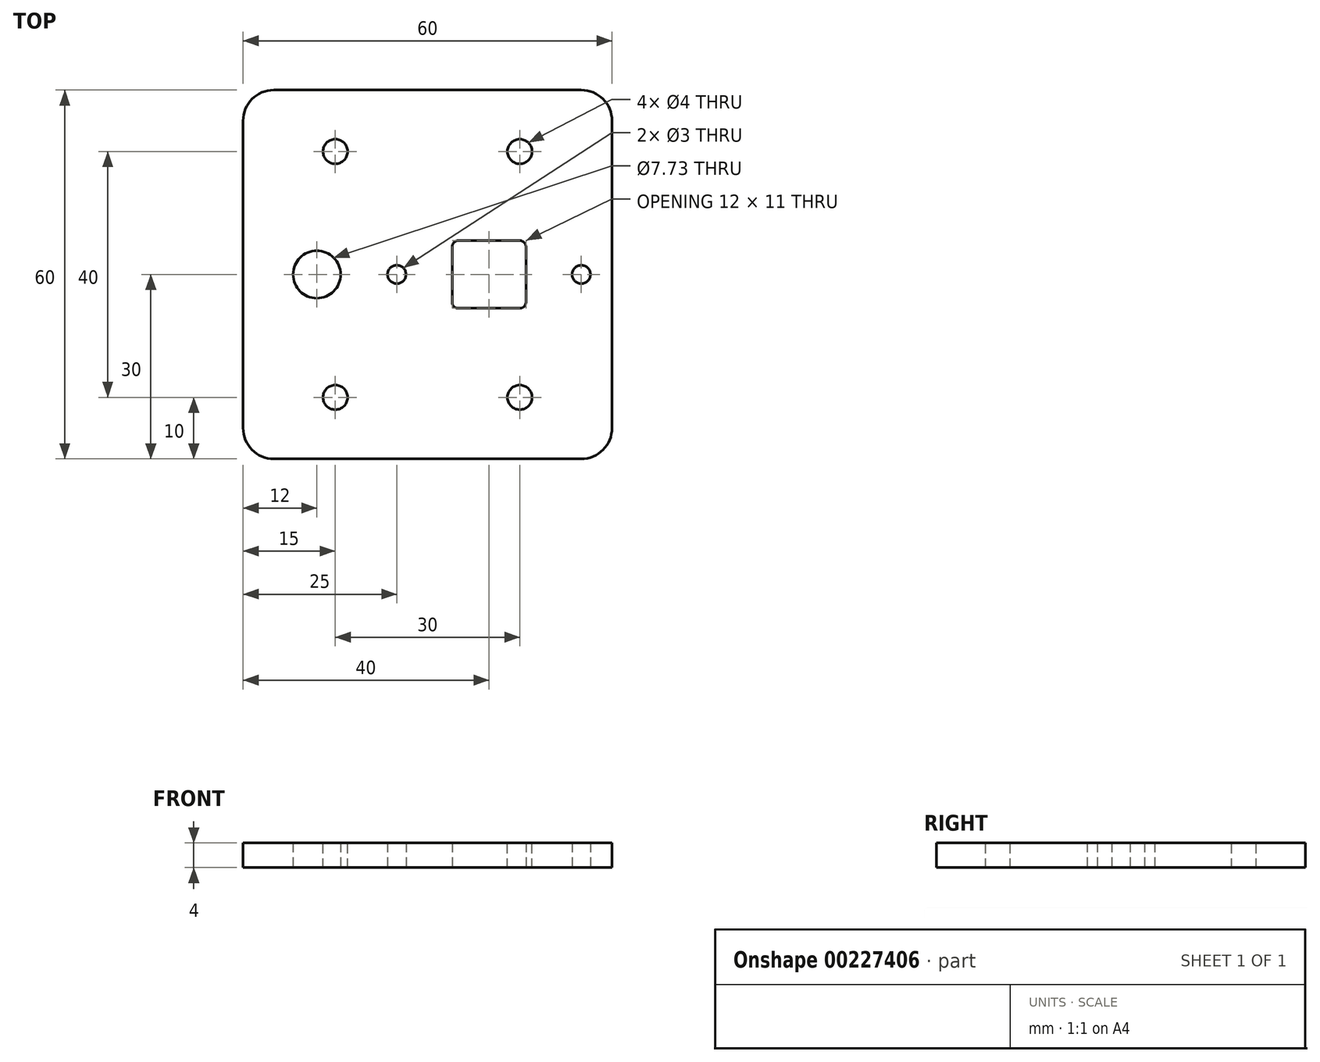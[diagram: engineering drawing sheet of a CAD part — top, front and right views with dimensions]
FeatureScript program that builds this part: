
annotation { "Feature Type Name" : "Feature", "Feature Type Description" : "" }
export const myFeature = defineFeature(function(context is Context, id is Id, definition is map)
    precondition{}
    {
        {
            var Q0;
            Q0=qCreatedBy(makeId("Top.planeOp"),FACE);
            var sketch = newSketch(context, id + "F0", { "sketchPlane" : qUnion([Q0])});
            skCircle(sketch, "E0", {"center": v(-18, 0) * mm, "radius": 3.86 * mm});
            skLineSegment(sketch, "E1.bottom", {"start": v(-30, 30) * mm, "end": v(30, 30) * mm});
            skLineSegment(sketch, "E1.top", {"start": v(-30, -30) * mm, "end": v(30, -30) * mm});
            skLineSegment(sketch, "E1.left", {"start": v(-30, 30) * mm, "end": v(-30, -30) * mm});
            skLineSegment(sketch, "E1.right", {"start": v(30, 30) * mm, "end": v(30, -30) * mm});
            skPoint(sketch, "E2", {"position": v(-30, 0) * mm});
            skPoint(sketch, "E3", {"position": v(0, 30) * mm});
            skCircle(sketch, "E4", {"center": v(-5, 0) * mm, "radius": 1.5 * mm});
            skCircle(sketch, "E5", {"center": v(25, 0) * mm, "radius": 1.5 * mm});
            skLineSegment(sketch, "E6.bottom", {"start": v(4, 5.5) * mm, "end": v(16, 5.5) * mm});
            skLineSegment(sketch, "E6.top", {"start": v(4, -5.5) * mm, "end": v(16, -5.5) * mm});
            skLineSegment(sketch, "E6.left", {"start": v(4, 5.5) * mm, "end": v(4, -5.5) * mm});
            skLineSegment(sketch, "E6.right", {"start": v(16, 5.5) * mm, "end": v(16, -5.5) * mm});
            skPoint(sketch, "E7", {"position": v(16, 0) * mm});
            skPoint(sketch, "E8", {"position": v(4, 0) * mm});
            skSolve(sketch);
        }
        {
            var Q0;
            Q0=makeQuery(id+"F0.imprint","IMPRINT",FACE,{"disambiguationData":[TD([[makeQuery(id+"F0.imprint","IMPRINT",EDGE,{"derivedFrom":sQuery(id+"F0.wireOp",EDGE,"E0")}),-1.0]])]});
            extrude(context, id + "F1", {"entities" : qUnion([Q0]), "depth" : 4 * mm});
        }
        {
            var Q0;
            Q0=makeQuery(id+"F1.opExtrude","CAP_FACE",FACE,{"disambiguationData":[OSD([sQuery(id+"F0.wireOp",EDGE,"E0"),sQuery(id+"F0.wireOp",EDGE,"E1.bottom"),sQuery(id+"F0.wireOp",EDGE,"E1.top"),sQuery(id+"F0.wireOp",EDGE,"E1.left"),sQuery(id+"F0.wireOp",EDGE,"E1.right"),sQuery(id+"F0.wireOp",EDGE,"E4"),sQuery(id+"F0.wireOp",EDGE,"E5"),sQuery(id+"F0.wireOp",EDGE,"E6.bottom"),sQuery(id+"F0.wireOp",EDGE,"E6.top"),sQuery(id+"F0.wireOp",EDGE,"E6.left"),sQuery(id+"F0.wireOp",EDGE,"E6.right")])],"isStart":false});
            var sketch = newSketch(context, id + "F2", { "sketchPlane" : qUnion([Q0])});
            skCircle(sketch, "E9", {"center": v(-15, 20) * mm, "radius": 2 * mm});
            skCircle(sketch, "E10", {"center": v(15, 20) * mm, "radius": 2 * mm});
            skCircle(sketch, "E11", {"center": v(-15, -20) * mm, "radius": 2 * mm});
            skCircle(sketch, "E12", {"center": v(15, -20) * mm, "radius": 2 * mm});
            skPoint(sketch, "E13", {"position": v(0, 30) * mm});
            skSolve(sketch);
        }
        {
            var Q0;
            Q0=makeQuery(id+"F2.imprint","IMPRINT",FACE,{"disambiguationData":[TD([[makeQuery(id+"F2.imprint","IMPRINT",EDGE,{"derivedFrom":sQuery(id+"F2.wireOp",EDGE,"E9")}),1.0]])]});
            var Q1;
            Q1=makeQuery(id+"F2.imprint","IMPRINT",FACE,{"disambiguationData":[TD([[makeQuery(id+"F2.imprint","IMPRINT",EDGE,{"derivedFrom":sQuery(id+"F2.wireOp",EDGE,"E10")}),1.0]])]});
            var Q2;
            Q2=makeQuery(id+"F2.imprint","IMPRINT",FACE,{"disambiguationData":[TD([[makeQuery(id+"F2.imprint","IMPRINT",EDGE,{"derivedFrom":sQuery(id+"F2.wireOp",EDGE,"E12")}),1.0]])]});
            var Q3;
            Q3=makeQuery(id+"F2.imprint","IMPRINT",FACE,{"disambiguationData":[TD([[makeQuery(id+"F2.imprint","IMPRINT",EDGE,{"derivedFrom":sQuery(id+"F2.wireOp",EDGE,"E11")}),1.0]])]});
            extrude(context, id + "F3", {"entities" : qUnion([Q0, Q1, Q2, Q3]), "operationType" : NewBodyOperationType.REMOVE, "oppositeDirection" : true, "depth" : 25 * mm});
        }
        {
            var Q0;
            Q0=makeQuery(id+"F1.opExtrude","SWEPT_EDGE",EDGE,{"disambiguationData":[OSD([sQuery(id+"F0.wireOp",EDGE,"E1.bottom"),sQuery(id+"F0.wireOp",EDGE,"E1.left")])]});
            var Q1;
            Q1=makeQuery(id+"F1.opExtrude","SWEPT_EDGE",EDGE,{"disambiguationData":[OSD([sQuery(id+"F0.wireOp",EDGE,"E1.top"),sQuery(id+"F0.wireOp",EDGE,"E1.left")])]});
            var Q2;
            Q2=makeQuery(id+"F1.opExtrude","SWEPT_EDGE",EDGE,{"disambiguationData":[OSD([sQuery(id+"F0.wireOp",EDGE,"E1.top"),sQuery(id+"F0.wireOp",EDGE,"E1.right")])]});
            var Q3;
            Q3=makeQuery(id+"F1.opExtrude","SWEPT_EDGE",EDGE,{"disambiguationData":[OSD([sQuery(id+"F0.wireOp",EDGE,"E1.bottom"),sQuery(id+"F0.wireOp",EDGE,"E1.right")])]});
            fillet(context, id + "F4", {"entities" : qUnion([Q0, Q1, Q2, Q3]), "radius" : 5 * mm, "tangentPropagation" : true, "allowEdgeOverflow" : false});
        }
        {
            var Q0;
            Q0=makeQuery(id+"F1.opExtrude","SWEPT_EDGE",EDGE,{"disambiguationData":[OSD([sQuery(id+"F0.wireOp",EDGE,"E6.bottom"),sQuery(id+"F0.wireOp",EDGE,"E6.left")])]});
            var Q1;
            Q1=makeQuery(id+"F1.opExtrude","SWEPT_EDGE",EDGE,{"disambiguationData":[OSD([sQuery(id+"F0.wireOp",EDGE,"E6.bottom"),sQuery(id+"F0.wireOp",EDGE,"E6.right")])]});
            var Q2;
            Q2=makeQuery(id+"F1.opExtrude","SWEPT_EDGE",EDGE,{"disambiguationData":[OSD([sQuery(id+"F0.wireOp",EDGE,"E6.top"),sQuery(id+"F0.wireOp",EDGE,"E6.right")])]});
            var Q3;
            Q3=makeQuery(id+"F1.opExtrude","SWEPT_EDGE",EDGE,{"disambiguationData":[OSD([sQuery(id+"F0.wireOp",EDGE,"E6.top"),sQuery(id+"F0.wireOp",EDGE,"E6.left")])]});
            fillet(context, id + "F5", {"entities" : qUnion([Q0, Q1, Q2, Q3]), "radius" : 1 * mm, "tangentPropagation" : true, "allowEdgeOverflow" : false});
        }
    });
